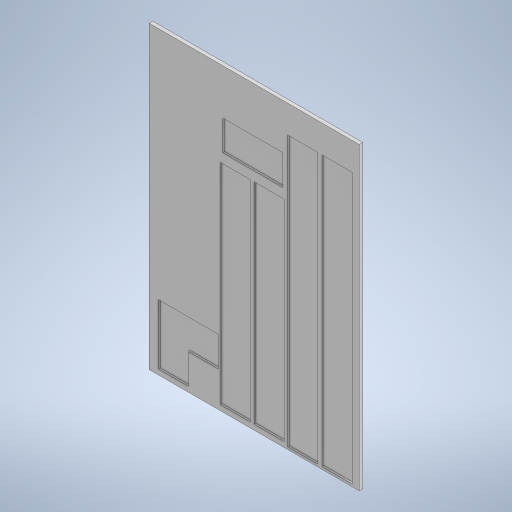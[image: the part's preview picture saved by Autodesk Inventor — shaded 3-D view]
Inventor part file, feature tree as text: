
AUTODESK INVENTOR PART (.ipt)
format: ipt  version: 2023 (Build 270158000, 158)  size: 267,264 bytes
history: native  units: mm
features: extrude x2, sketch x2, other x1
ambient origin geometry x8: Origin, YZ Plane, XZ Plane, XY Plane, X Axis, Y Axis, Z Axis, Center Point
bodies: Body1 (feature_tree)
feature tree (5):
  other  "Sólido1"
  extrude  "Extrusión1"  Depth=500.0mm
  extrude  "Extrusión2"  Depth=15.3mm
  sketch  "Boceto1"  dims[d0=350.0mm d1=500.0mm]
  sketch  "Boceto2"  dims[d2=6.0mm d3=0.0mm d4=15.3mm d5=8.69mm d6=100.0mm d7=100.0mm d8=50.0mm d9=50.0mm d10=53.0mm d11=50.0mm d12=349.9mm d13=6.56mm d14=50.0mm d15=349.9mm d16=6.0mm d17=4.61mm d18=50.0mm d19=450.0mm d20=7.15mm d21=50.0mm d22=450.0mm d23=2.0mm d24=16.0mm d25=100.0mm d26=50.0mm d27=3.0mm d28=0.0mm]
